# Revit family: ADB Electric cooktops cupboard 800 IX
name_source: partatom
category: Equipement spécialisé
units: mm (PartAtom-declared; Revit-internal decimal feet)

## family parameters
Basée sur le plan de construction = Non
Conserver l'orientation des annotations = Non
Cote de connecteur circulaire = Utiliser le diamètre
Couper avec des vides une fois chargée = Non
Numéro OmniClass = 23.40.40.14.17.11
Partagée = Non
Repère de localisation dans la pièce = Non
Titre OmniClass = Cookers, Ovens, Stoves
Toujours verticalement = Oui
Type d'élément = Normal

## types (2) — shared parameters
C = 140 mm  [stored 0.459318 ft]
Commentaires du type = Ambassade range - Cupboards - Electric cooktops
D = 765 mm  [stored 2.50984 ft]
Fabricant = Société Industrielle de Lacanche
URL = https://www.ambassade-de-bourgogne.com
URL Cutsheet = https://www.ambassade-de-bourgogne.com
zero-valued in all types: Elévation par défaut

## per-type parameters (varying)
| type | Description | Electric power | Operational Current | Panneau commande | Table |
| CME 833 IX | 2x3kW+3,6kW induction ring electric cupboard | 9600 W | 21 A | Ecran Tactile 1 feu | 3-4 foyers induction : 3 foyers |
| CME 843 IX | 4x3 kW induction ring electric cupboard | 12000 W | 26 A | Ecran Tactile | 3-4 foyers induction : 4 foyers |

note: column(s) folded — value = type name in every type: Modèle

note: [stored X ft] marks values corroborated as IEEE doubles in the binary element streams (Revit-internal decimal feet)
